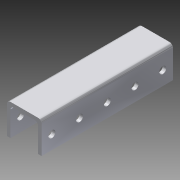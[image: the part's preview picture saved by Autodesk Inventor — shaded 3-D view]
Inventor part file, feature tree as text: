
AUTODESK INVENTOR PART (.ipt)
format: ipt  version: 2015 (Build 190159000, 159)  size: 234,496 bytes
history: native  units: in
note: dims shown in document units (in); Inventor stores cm internally (conversion verified against a paired STEP export)
features: extrude x2, sketch x2, pattern_linear x1
ambient origin geometry x8: Origin, YZ Plane, XZ Plane, XY Plane, X Axis, Y Axis, Z Axis, Center Point
bodies: Solid1 (feature_tree)
feature tree (5):
  extrude  "Extrusion1"  Depth=4.74in
  extrude  "Extrusion4"  Depth=0.5in
  pattern_linear  "Rectangular Pattern3"  Spacing1=0.0in  [1 undecoded]
  sketch  "Sketch1"  dims[d0=1.13in d1=1.25in d2=0.125in d3=0.125in d4=0.125in d5=4.74in]
  sketch  "Sketch4"  dims[d6=0.0in d35=0.5in d36=0.0in d37=0.25in d38=1.0in d39=0.0in d40=7.874in d42=1.0in d43=7.874in d45=1.0in]
note: 1 required parameter value undecoded (feature->parameter linkage not recoverable at this tier; creation-order binding heuristic only, values carry confidence <= 0.55)
